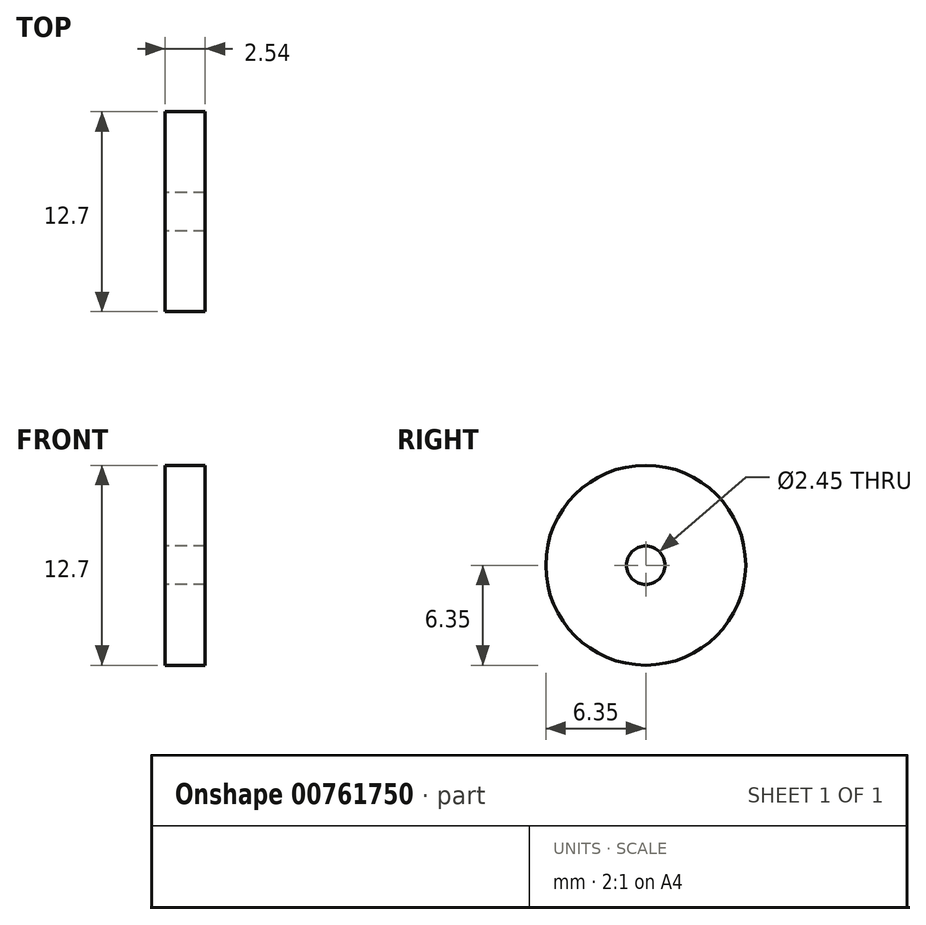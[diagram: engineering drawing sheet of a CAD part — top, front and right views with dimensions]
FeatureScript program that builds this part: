
annotation { "Feature Type Name" : "Feature", "Feature Type Description" : "" }
export const myFeature = defineFeature(function(context is Context, id is Id, definition is map)
    precondition{}
    {
        {
            var Q0;
            Q0=qCreatedBy(makeId("Right.planeOp"),FACE);
            var sketch = newSketch(context, id + "F0", { "sketchPlane" : qUnion([Q0])});
            skCircle(sketch, "E0", {"center": v(0, 0) * mm, "radius": 6.35 * mm});
            skCircle(sketch, "E1", {"center": v(0, 0) * mm, "radius": 1.22 * mm});
            skSolve(sketch);
        }
        {
            var Q0;
            Q0=makeQuery(id+"F0.imprint","IMPRINT",FACE,{"disambiguationData":[TD([[makeQuery(id+"F0.imprint","IMPRINT",EDGE,{"derivedFrom":sQuery(id+"F0.wireOp",EDGE,"E0")}),1.0]])]});
            extrude(context, id + "F1", {"entities" : qUnion([Q0]), "depth" : 2.54 * mm, "offsetDistance" : 25.4 * mm});
        }
    });
